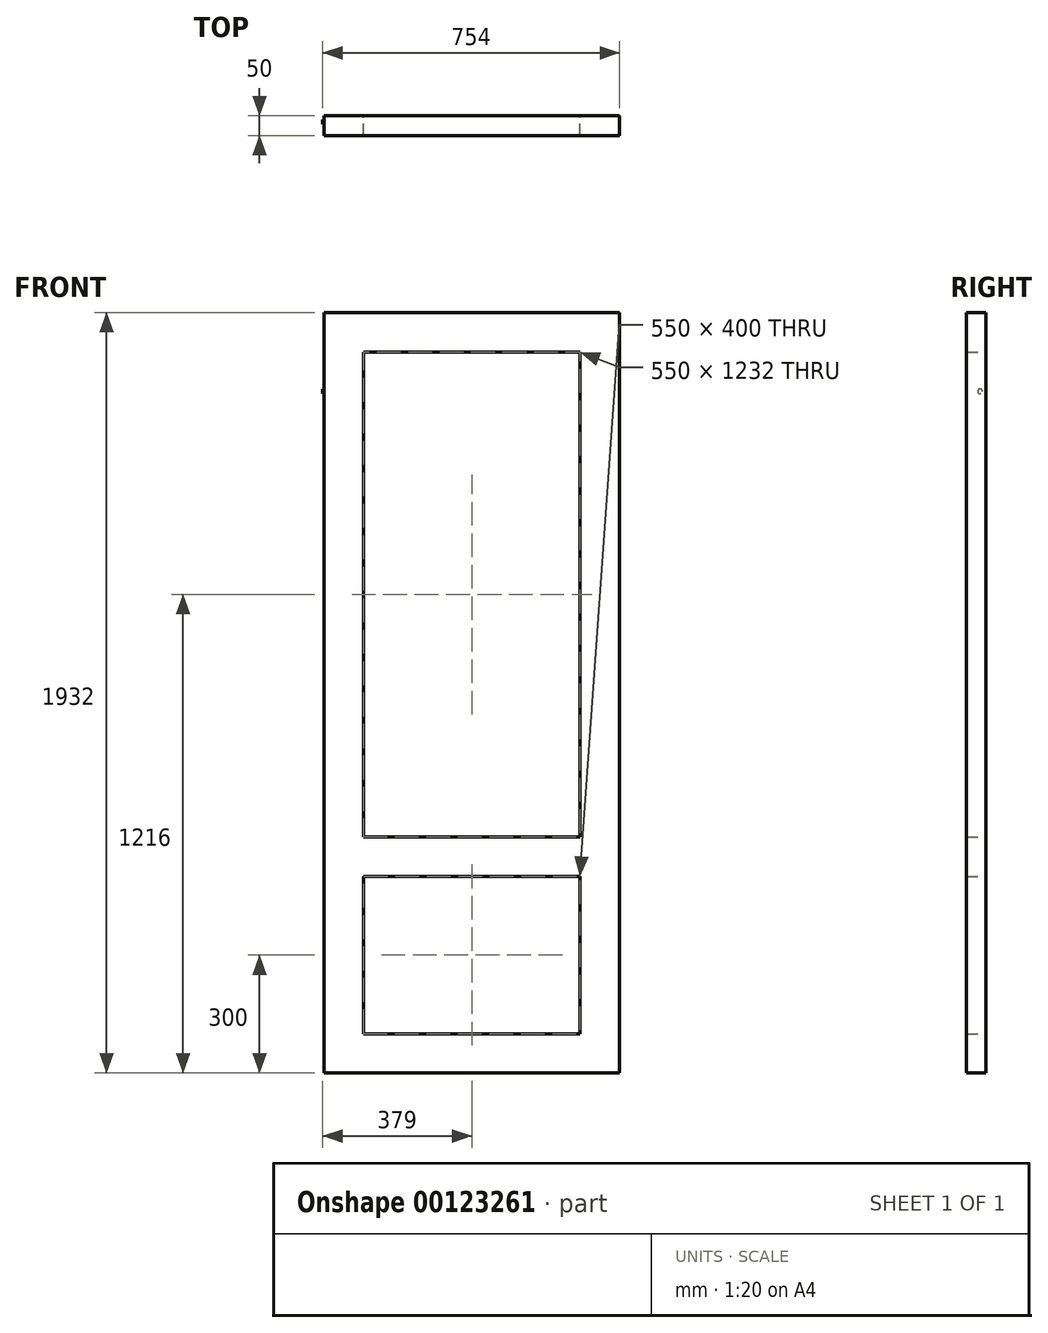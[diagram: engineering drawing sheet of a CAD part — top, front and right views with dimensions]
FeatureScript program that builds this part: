
annotation { "Feature Type Name" : "Feature", "Feature Type Description" : "" }
export const myFeature = defineFeature(function(context is Context, id is Id, definition is map)
    precondition{}
    {
        {
            var Q0;
            Q0=qCreatedBy(makeId("Front.planeOp"),FACE);
            var sketch = newSketch(context, id + "F0", { "sketchPlane" : qUnion([Q0])});
            skLineSegment(sketch, "E0.bottom", {"start": v(-375, 966) * mm, "end": v(375, 966) * mm});
            skLineSegment(sketch, "E0.top", {"start": v(-375, -966) * mm, "end": v(375, -966) * mm});
            skLineSegment(sketch, "E0.left", {"start": v(-375, 966) * mm, "end": v(-375, -966) * mm});
            skLineSegment(sketch, "E0.right", {"start": v(375, 966) * mm, "end": v(375, -966) * mm});
            skLineSegment(sketch, "E1.0", {"start": v(-275, 866) * mm, "end": v(275, 866) * mm});
            skLineSegment(sketch, "E1.1", {"start": v(-275, 866) * mm, "end": v(-275, -866) * mm});
            skLineSegment(sketch, "E1.2", {"start": v(-275, -866) * mm, "end": v(275, -866) * mm});
            skLineSegment(sketch, "E1.3", {"start": v(275, 866) * mm, "end": v(275, -866) * mm});
            skLineSegment(sketch, "E2.bottom", {"start": v(-275, -366) * mm, "end": v(275, -366) * mm});
            skLineSegment(sketch, "E2.top", {"start": v(-275, -466) * mm, "end": v(275, -466) * mm});
            skLineSegment(sketch, "E2.left", {"start": v(-275, -366) * mm, "end": v(-275, -466) * mm});
            skLineSegment(sketch, "E2.right", {"start": v(275, -366) * mm, "end": v(275, -466) * mm});
            skSolve(sketch);
        }
        {
            var Q0;
            Q0=makeQuery(id+"F0.imprint","IMPRINT",FACE,{"disambiguationData":[TD([[makeQuery(id+"F0.imprint","IMPRINT",EDGE,{"derivedFrom":sQuery(id+"F0.wireOp",EDGE,"E0.bottom")}),-1.0]])]});
            var Q1;
            Q1=makeQuery(id+"F0.imprint","IMPRINT",FACE,{"disambiguationData":[TD([[makeQuery(id+"F0.imprint","IMPRINT",EDGE,{"derivedFrom":sQuery(id+"F0.wireOp",EDGE,"E2.bottom")}),-1.0]])]});
            extrude(context, id + "F1", {"entities" : qUnion([Q0, Q1]), "endBound" : BoundingType.SYMMETRIC, "depth" : 50 * mm});
        }
        {
            var Q0;
            Q0=qCreatedBy(makeId("Right.planeOp"),FACE);
            cPlane(context, id + "F2", {"entities" : qUnion([Q0]), "cplaneType" : CPlaneType.OFFSET, "offset" : 375 * mm, "oppositeDirection" : true, "width" : 150 * mm, "height" : 150 * mm});
        }
        {
            var Q0;
            Q0=qCreatedBy(id+"F2.planeOp",FACE);
            var sketch = newSketch(context, id + "F3", { "sketchPlane" : qUnion([Q0])});
            skCircle(sketch, "E3", {"center": v(10, 766) * mm, "radius": 6 * mm});
            skCircle(sketch, "E4.MirrorC", {"center": v(10, -766) * mm, "radius": 6 * mm});
            skSolve(sketch);
        }
        {
            var Q0;
            Q0=makeQuery(id+"F3.imprint","IMPRINT",FACE,{"disambiguationData":[TD([[makeQuery(id+"F3.imprint","IMPRINT",EDGE,{"derivedFrom":sQuery(id+"F3.wireOp",EDGE,"E3")}),1.0]])]});
            var Q1;
            Q1=makeQuery(id+"F3.imprint","IMPRINT",FACE,{"disambiguationData":[TD([[makeQuery(id+"F3.imprint","IMPRINT",EDGE,{"derivedFrom":sQuery(id+"F3.wireOp",EDGE,"E4.MirrorC")}),-1.0]])]});
            extrude(context, id + "F4", {"entities" : qUnion([Q0, Q1]), "operationType" : NewBodyOperationType.ADD, "oppositeDirection" : true, "depth" : 4 * mm});
        }
    });
